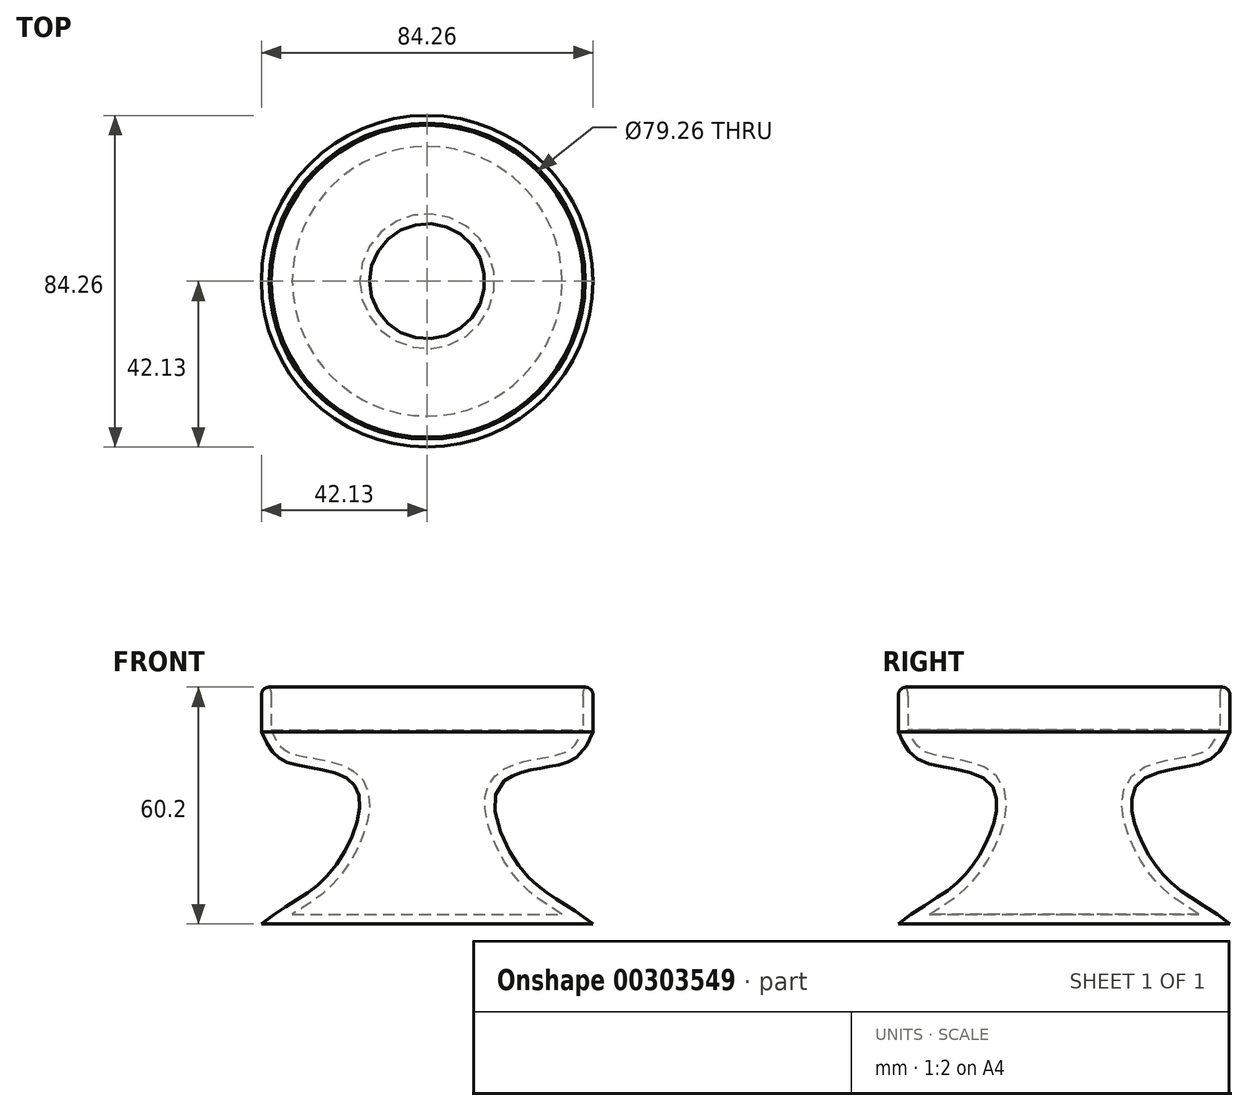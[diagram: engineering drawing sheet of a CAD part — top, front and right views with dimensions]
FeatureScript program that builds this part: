
annotation { "Feature Type Name" : "Feature", "Feature Type Description" : "" }
export const myFeature = defineFeature(function(context is Context, id is Id, definition is map)
    precondition{}
    {
        {
            var Q0;
            Q0=qCreatedBy(makeId("Front.planeOp"),FACE);
            var sketch = newSketch(context, id + "F0", { "sketchPlane" : qUnion([Q0])});
            skLineSegment(sketch, "E0", {"start": v(0, 0) * mm, "end": v(0, 60.2) * mm});
            skLineSegment(sketch, "E1", {"start": v(0, 60.2) * mm, "end": v(42.13, 60.2) * mm});
            skLineSegment(sketch, "E2", {"start": v(42.13, 60.2) * mm, "end": v(42.13, 48.8) * mm});
            skLineSegment(sketch, "E3", {"start": v(42.13, 0) * mm, "end": v(-10.43, 0) * mm});
            skFitSpline(sketch, "E4", {"points": [v(42.13, 48.8) * mm, v(34.2, 40.68) * mm, v(18.17, 34.88) * mm, v(24.54, 13.24) * mm, v(42.13, 0) * mm], "startDerivative": vector(-33.03, -77.3) * mm, "endDerivative": vector(74.47, -60.96) * mm});
            skSolve(sketch);
        }
        {
            var Q0;
            {var subQ1=sQuery(id+"F0.wireOp",EDGE,"E0");Q0=makeQuery(id+"F0.imprint","IMPRINT",FACE,{"disambiguationData":[TD([[makeQuery(id+"F0.imprint","IMPRINT",EDGE,{"derivedFrom":subQ1}),-1.0]])]});}
            var Q1;
            Q1=sQuery(id+"F0.wireOp",EDGE,"E0");
            revolve(context, id + "F1", {"entities" : qUnion([Q0]), "axis" : qUnion([Q1]), "revolveType" : RevolveType.FULL});
        }
        {
            var Q0;
            Q0=makeQuery(id+"F1.opRevolve","SWEPT_FACE",FACE,{"disambiguationData":[OSD([sQuery(id+"F0.wireOp",EDGE,"E1")])]});
            shell(context, id + "F2", {"entities" : qUnion([Q0]), "thickness" : 2.5 * mm});
        }
        {
            var Q0;
            Q0=makeQuery(id+"F1.opRevolve","SWEPT_EDGE",EDGE,{"disambiguationData":[OSD([sQuery(id+"F0.wireOp",EDGE,"E1"),sQuery(id+"F0.wireOp",EDGE,"E2")])]});
            fillet(context, id + "F3", {"entities" : qUnion([Q0]), "radius" : 2 * mm, "tangentPropagation" : true, "allowEdgeOverflow" : false});
        }
        {
            var Q0;
            Q0=makeQuery(id+"F2.opShell","OFFSET_EDGE",EDGE,{"disambiguationData":[OSD([sQuery(id+"F0.wireOp",EDGE,"E1"),sQuery(id+"F0.wireOp",EDGE,"E2")])]});
            fillet(context, id + "F4", {"entities" : qUnion([Q0]), "radius" : 5 * mm, "tangentPropagation" : true, "allowEdgeOverflow" : false});
        }
    });
